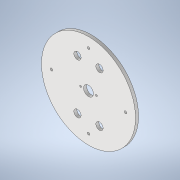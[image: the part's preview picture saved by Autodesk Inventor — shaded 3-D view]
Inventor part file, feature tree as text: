
AUTODESK INVENTOR PART (.ipt)
format: ipt  version: 2022 (Build 260153000, 153)  size: 138,240 bytes
history: native  units: mm
features: extrude x1
ambient origin geometry x8: Origin, YZ Plane, XZ Plane, XY Plane, X Axis, Y Axis, Z Axis, Center Point
bodies: Solid1 (feature_tree)
feature tree (1):
  extrude  "Extrusion1"  Depth=94.0mm
